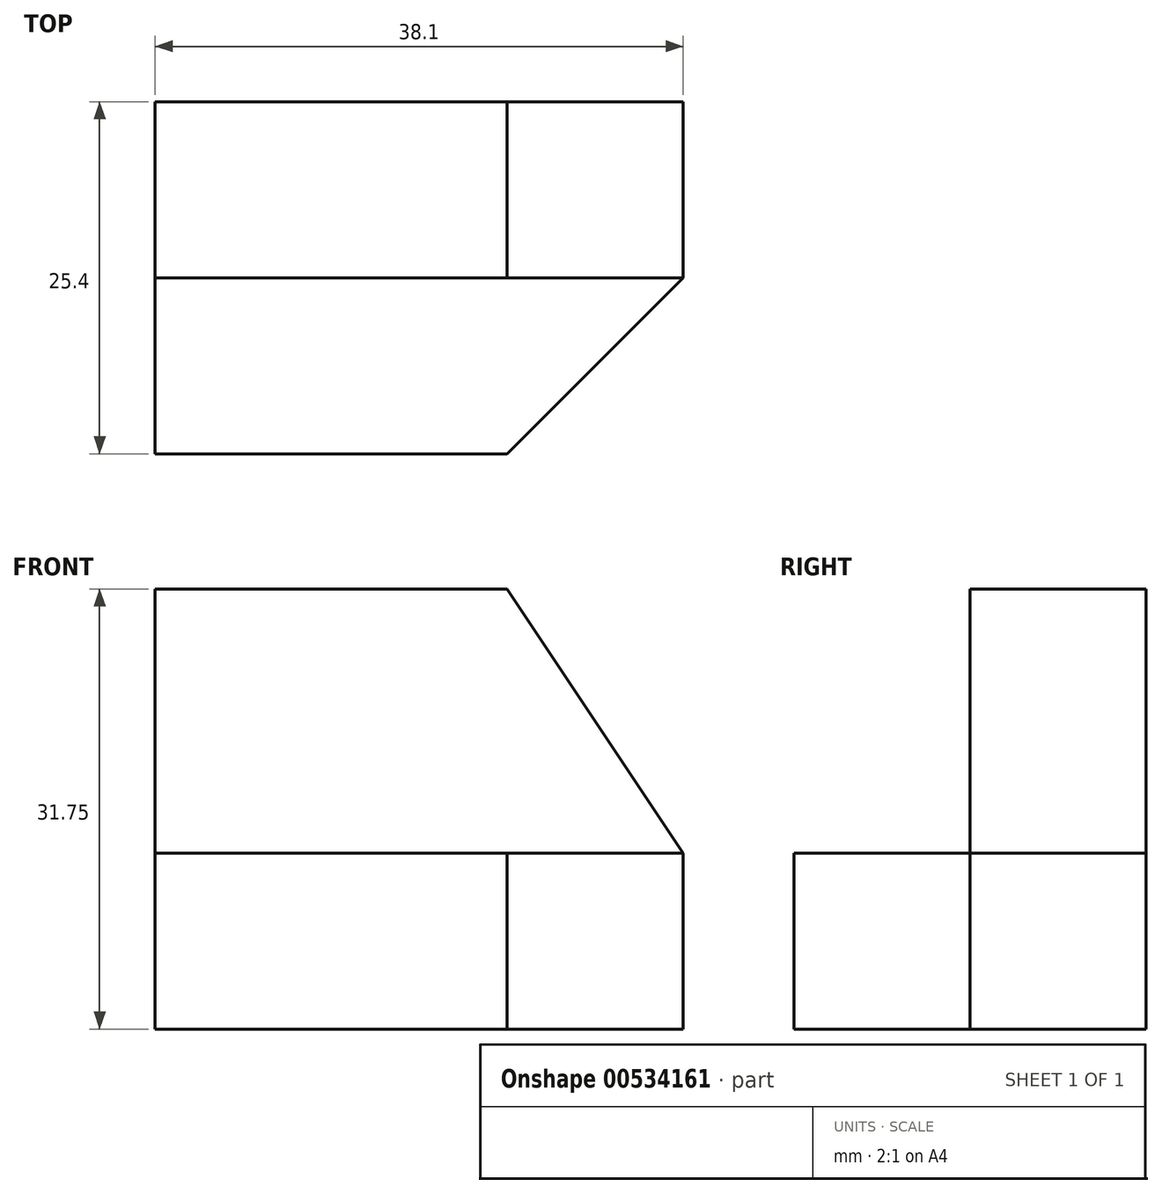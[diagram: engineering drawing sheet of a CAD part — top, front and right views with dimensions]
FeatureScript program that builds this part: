
annotation { "Feature Type Name" : "Feature", "Feature Type Description" : "" }
export const myFeature = defineFeature(function(context is Context, id is Id, definition is map)
    precondition{}
    {
        {
            var Q0;
            Q0=qCreatedBy(makeId("Front.planeOp"),FACE);
            var sketch = newSketch(context, id + "F0", { "sketchPlane" : qUnion([Q0])});
            skLineSegment(sketch, "E0", {"start": v(0, 0) * mm, "end": v(0, 31.75) * mm});
            skLineSegment(sketch, "E1", {"start": v(0, 31.75) * mm, "end": v(38.1, 31.75) * mm});
            skLineSegment(sketch, "E2", {"start": v(38.1, 31.75) * mm, "end": v(38.1, 0) * mm});
            skLineSegment(sketch, "E3", {"start": v(38.1, 0) * mm, "end": v(0, 0) * mm});
            skSolve(sketch);
        }
        {
            var Q0;
            Q0=makeQuery(id+"F0.imprint","IMPRINT",FACE,{"disambiguationData":[TD([[makeQuery(id+"F0.imprint","IMPRINT",EDGE,{"derivedFrom":sQuery(id+"F0.wireOp",EDGE,"E0")}),-1.0]])]});
            extrude(context, id + "F1", {"entities" : qUnion([Q0]), "depth" : 25.4 * mm, "offsetDistance" : 25.4 * mm});
        }
        {
            var Q0;
            Q0=makeQuery(id+"F1.opExtrude","SWEPT_FACE",FACE,{"disambiguationData":[OSD([sQuery(id+"F0.wireOp",EDGE,"E1")])]});
            var sketch = newSketch(context, id + "F2", { "sketchPlane" : qUnion([Q0])});
            skLineSegment(sketch, "E4", {"start": v(0, -12.7) * mm, "end": v(38.1, -12.7) * mm});
            skLineSegment(sketch, "E5", {"start": v(38.1, -12.7) * mm, "end": v(25.4, -25.4) * mm});
            skSolve(sketch);
        }
        {
            var Q0;
            {var subQ0=sQuery(id+"F2.wireOp",EDGE,"E5");Q0=makeQuery(id+"F2.imprint","IMPRINT",FACE,{"disambiguationData":[TD([[makeQuery(id+"F2.imprint","IMPRINT",EDGE,{"derivedFrom":subQ0}),1.0]])]});}
            extrude(context, id + "F3", {"entities" : qUnion([Q0]), "operationType" : NewBodyOperationType.REMOVE, "oppositeDirection" : true, "depth" : 31.75 * mm, "offsetDistance" : 25.4 * mm});
        }
        {
            var Q0;
            Q0=makeQuery(id+"F1.opExtrude","SWEPT_FACE",FACE,{"disambiguationData":[OSD([sQuery(id+"F0.wireOp",EDGE,"E1")])]});
            var sketch = newSketch(context, id + "F4", { "sketchPlane" : qUnion([Q0])});
            skLineSegment(sketch, "E6", {"start": v(38.1, -12.7) * mm, "end": v(0, -12.7) * mm});
            skSolve(sketch);
        }
        {
            var Q0;
            Q0 = qSketchRegion(id + "F4", true);
            var Q1;
            {var subQ0=sQuery(id+"F4.wireOp",EDGE,"E6");Q1=makeQuery(id+"F4.imprint","IMPRINT",FACE,{"disambiguationData":[TD([[makeQuery(id+"F4.imprint","IMPRINT",EDGE,{"derivedFrom":subQ0}),1.0]])]});}
            extrude(context, id + "F5", {"entities" : qUnion([Q0, Q1]), "operationType" : NewBodyOperationType.REMOVE, "oppositeDirection" : true, "depth" : 19.05 * mm, "offsetDistance" : 25.4 * mm});
        }
        {
            var Q0;
            Q0=makeQuery(id+"F5.boolean.opBoolean","COPY",FACE,{"derivedFrom":makeQuery(id+"F5.opExtrude","SWEPT_FACE",FACE,{"disambiguationData":[OSD([sQuery(id+"F4.wireOp",EDGE,"E6")])]})});
            var sketch = newSketch(context, id + "F6", { "sketchPlane" : qUnion([Q0])});
            skLineSegment(sketch, "E7", {"start": v(38.1, 12.7) * mm, "end": v(25.4, 31.75) * mm});
            skSolve(sketch);
        }
        {
            var Q0;
            {var subQ0=sQuery(id+"F6.wireOp",EDGE,"E7");Q0=makeQuery(id+"F6.imprint","IMPRINT",FACE,{"disambiguationData":[TD([[makeQuery(id+"F6.imprint","IMPRINT",EDGE,{"derivedFrom":subQ0}),-1.0]])]});}
            extrude(context, id + "F7", {"entities" : qUnion([Q0]), "operationType" : NewBodyOperationType.REMOVE, "oppositeDirection" : true, "depth" : 12.7 * mm, "offsetDistance" : 25.4 * mm});
        }
    });
